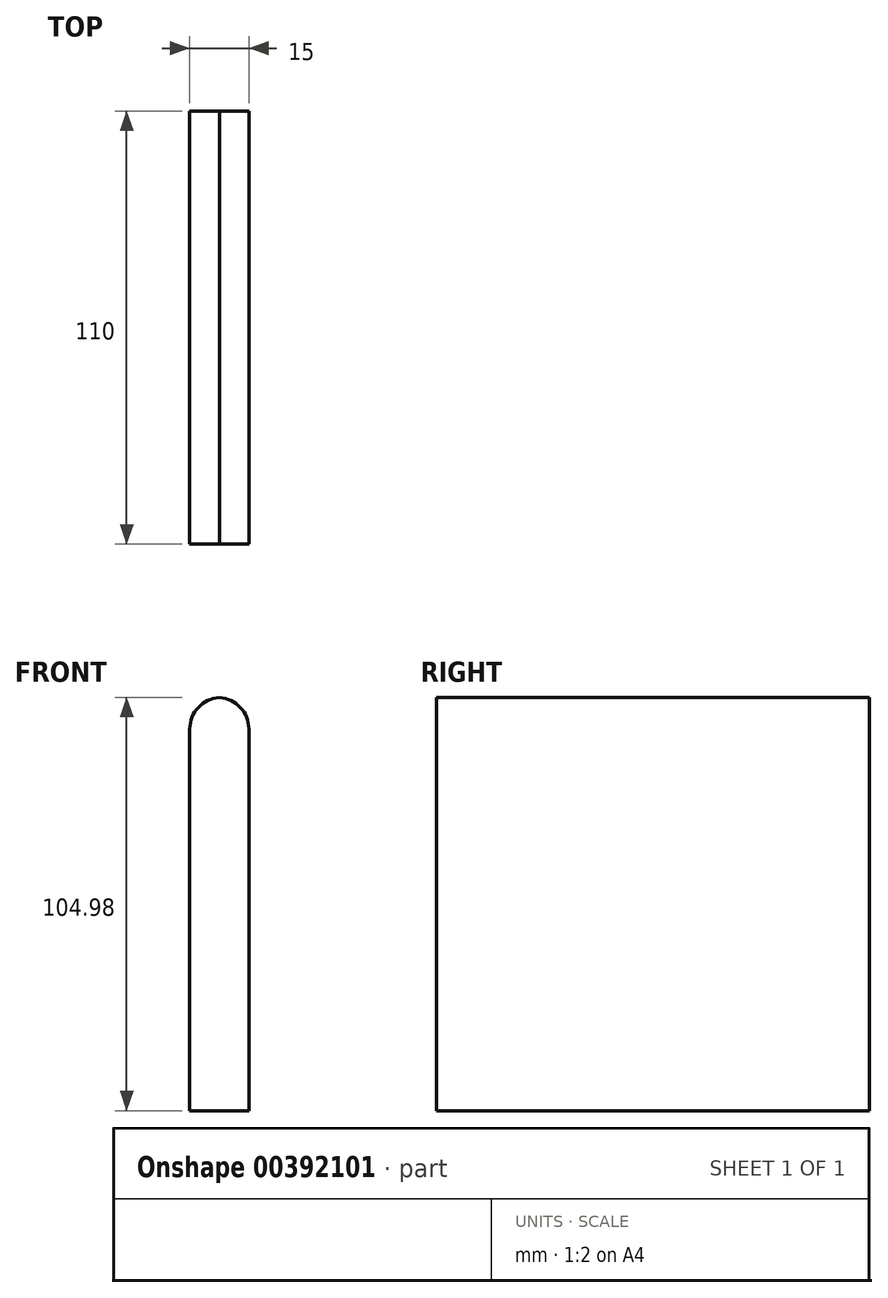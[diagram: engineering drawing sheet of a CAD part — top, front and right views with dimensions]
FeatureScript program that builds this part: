
annotation { "Feature Type Name" : "Feature", "Feature Type Description" : "" }
export const myFeature = defineFeature(function(context is Context, id is Id, definition is map)
    precondition{}
    {
        {
            var Q0;
            Q0=qCreatedBy(makeId("Top.planeOp"),FACE);
            var sketch = newSketch(context, id + "F0", { "sketchPlane" : qUnion([Q0])});
            skLineSegment(sketch, "E0.bottom", {"start": v(-5.87, 54.8) * mm, "end": v(9.13, 54.8) * mm});
            skLineSegment(sketch, "E0.top", {"start": v(-5.87, -55.2) * mm, "end": v(9.13, -55.2) * mm});
            skLineSegment(sketch, "E0.left", {"start": v(-5.87, 54.8) * mm, "end": v(-5.87, -55.2) * mm});
            skLineSegment(sketch, "E0.right", {"start": v(9.13, 54.8) * mm, "end": v(9.13, -55.2) * mm});
            skSolve(sketch);
        }
        {
            var Q0;
            Q0=makeQuery(id+"F0.imprint","IMPRINT",FACE,{"disambiguationData":[TD([[makeQuery(id+"F0.imprint","IMPRINT",EDGE,{"derivedFrom":sQuery(id+"F0.wireOp",EDGE,"E0.bottom")}),-1.0]])]});
            extrude(context, id + "F1", {"entities" : qUnion([Q0]), "depth" : 105 * mm});
        }
        {
            var Q0;
            Q0=makeQuery(id+"F1.opExtrude","CAP_EDGE",EDGE,{"disambiguationData":[OSD([sQuery(id+"F0.wireOp",EDGE,"E0.left")])],"isStart":false});
            var Q1;
            Q1=makeQuery(id+"F1.opExtrude","CAP_EDGE",EDGE,{"disambiguationData":[OSD([sQuery(id+"F0.wireOp",EDGE,"E0.right")])],"isStart":false});
            fillet(context, id + "F2", {"entities" : qUnion([Q0, Q1]), "radius" : 8 * mm, "tangentPropagation" : true, "allowEdgeOverflow" : false});
        }
    });
